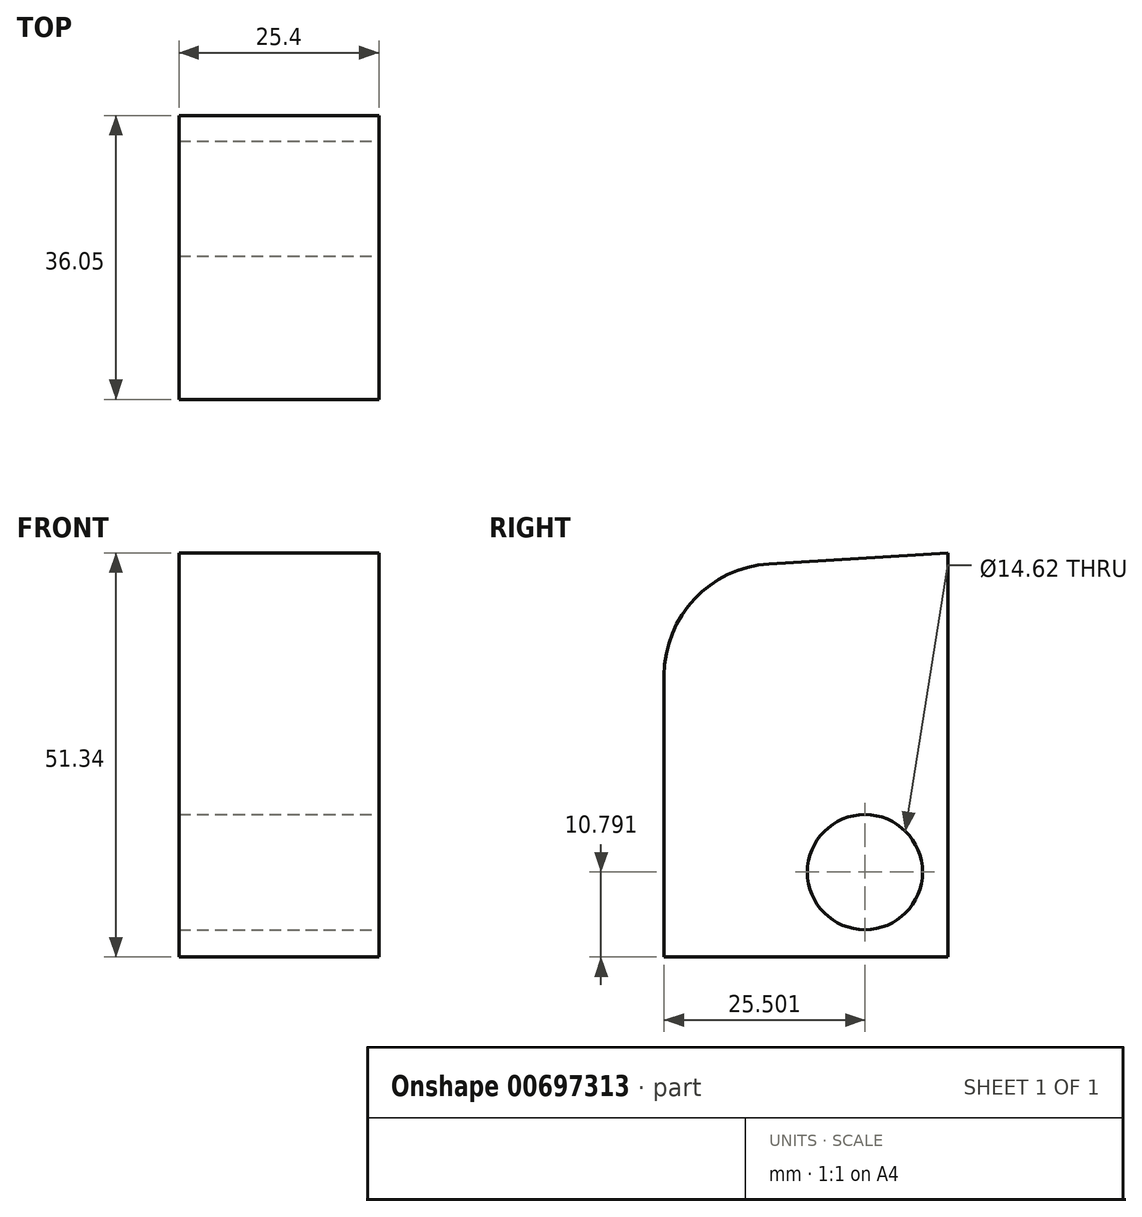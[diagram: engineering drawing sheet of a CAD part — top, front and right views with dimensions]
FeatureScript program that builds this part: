
annotation { "Feature Type Name" : "Feature", "Feature Type Description" : "" }
export const myFeature = defineFeature(function(context is Context, id is Id, definition is map)
    precondition{}
    {
        {
            var Q0;
            Q0=qCreatedBy(makeId("Right.planeOp"),FACE);
            var sketch = newSketch(context, id + "F0", { "sketchPlane" : qUnion([Q0])});
            skLineSegment(sketch, "E0", {"start": v(-56.18, 28.8) * mm, "end": v(-56.18, -7) * mm});
            skLineSegment(sketch, "E1", {"start": v(-56.18, -7) * mm, "end": v(-20.13, -7) * mm});
            skLineSegment(sketch, "E2", {"start": v(-20.13, -7) * mm, "end": v(-20.13, 44.33) * mm});
            skLineSegment(sketch, "E3", {"start": v(-20.13, 44.33) * mm, "end": v(-42.89, 42.92) * mm});
            skPoint(sketch, "E4.visualSharp", {"position": v(-56.18, 42.1) * mm});
            skArc(sketch, "E4.filletArc", {"start": v(-42.89, 42.92) * mm, "mid": v(-52.33, 38.5) * mm, "end": v(-56.18, 28.8) * mm});
            skSolve(sketch);
        }
        {
            var Q0;
            Q0=makeQuery(id+"F0.imprint","IMPRINT",FACE,{"disambiguationData":[TD([[makeQuery(id+"F0.imprint","IMPRINT",EDGE,{"derivedFrom":sQuery(id+"F0.wireOp",EDGE,"E0")}),1.0]])]});
            extrude(context, id + "F1", {"entities" : qUnion([Q0]), "oppositeDirection" : true, "depth" : 25.4 * mm, "offsetDistance" : 25.4 * mm});
        }
        {
            var Q0;
            Q0=qCreatedBy(makeId("Right.planeOp"),FACE);
            var sketch = newSketch(context, id + "F2", { "sketchPlane" : qUnion([Q0])});
            skCircle(sketch, "E5", {"center": v(-30.68, 3.78) * mm, "radius": 7.31 * mm});
            skSolve(sketch);
        }
        {
            var Q0;
            Q0 = qSketchRegion(id + "F2", true);
            extrude(context, id + "F3", {"entities" : qUnion([Q0]), "operationType" : NewBodyOperationType.REMOVE, "oppositeDirection" : true, "depth" : 25.4 * mm, "offsetDistance" : 25.4 * mm});
        }
    });
